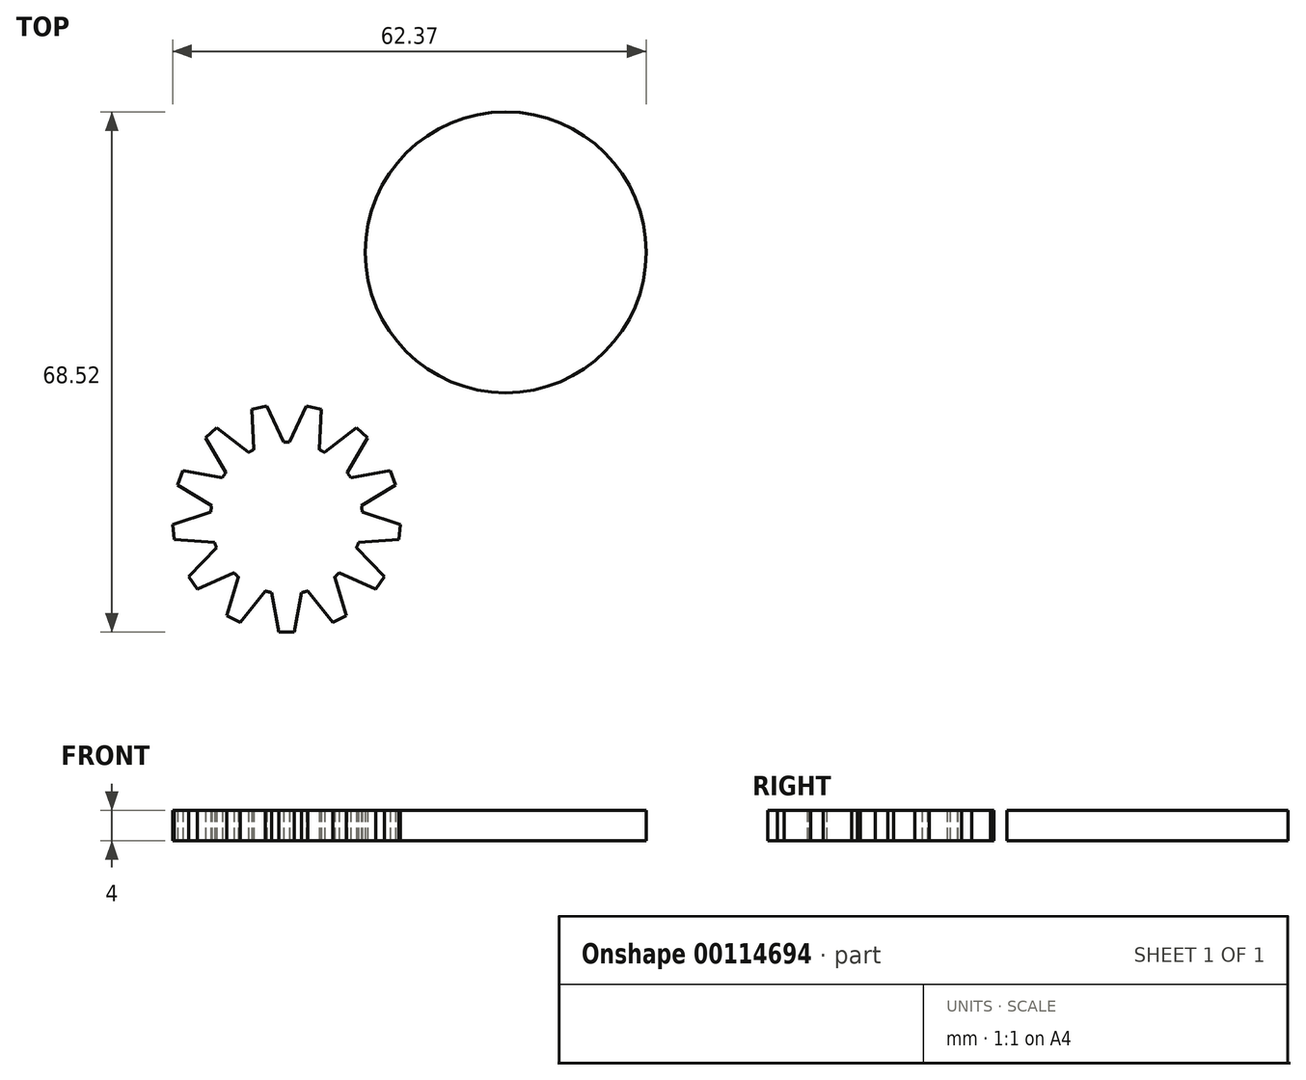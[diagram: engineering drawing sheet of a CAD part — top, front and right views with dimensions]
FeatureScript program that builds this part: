
annotation { "Feature Type Name" : "Feature", "Feature Type Description" : "" }
export const myFeature = defineFeature(function(context is Context, id is Id, definition is map)
    precondition{}
    {
        {
            var Q0;
            Q0=qCreatedBy(makeId("Top.planeOp"),FACE);
            var sketch = newSketch(context, id + "F0", { "sketchPlane" : qUnion([Q0])});
            skCircle(sketch, "E0", {"center": v(0, 0) * mm, "radius": 10 * mm});
            skLineSegment(sketch, "E1", {"start": v(0, -10) * mm, "end": v(0, -15) * mm});
            skLineSegment(sketch, "E2", {"start": v(0, -15) * mm, "end": v(-1, -15) * mm});
            skLineSegment(sketch, "E3", {"start": v(-1, -15) * mm, "end": v(-2, -9.8) * mm});
            skLineSegment(sketch, "E4", {"start": v(0, -15) * mm, "end": v(1, -15) * mm});
            skLineSegment(sketch, "E5", {"start": v(1, -15) * mm, "end": v(2, -9.8) * mm});
            skLineSegment(sketch, "E6.1.0", {"start": v(6.09, -13.75) * mm, "end": v(2.78, -9.6) * mm});
            skLineSegment(sketch, "E6.1.1", {"start": v(7.86, -12.82) * mm, "end": v(6.32, -7.75) * mm});
            skLineSegment(sketch, "E6.1.2", {"start": v(6.97, -13.28) * mm, "end": v(7.86, -12.82) * mm});
            skLineSegment(sketch, "E6.1.3", {"start": v(6.97, -13.28) * mm, "end": v(6.09, -13.75) * mm});
            skLineSegment(sketch, "E6.2.0", {"start": v(11.78, -9.34) * mm, "end": v(6.93, -7.21) * mm});
            skLineSegment(sketch, "E6.2.1", {"start": v(12.91, -7.7) * mm, "end": v(9.2, -3.92) * mm});
            skLineSegment(sketch, "E6.2.2", {"start": v(12.34, -8.52) * mm, "end": v(12.91, -7.7) * mm});
            skLineSegment(sketch, "E6.2.3", {"start": v(12.34, -8.52) * mm, "end": v(11.78, -9.34) * mm});
            skLineSegment(sketch, "E6.3.0", {"start": v(14.77, -2.8) * mm, "end": v(9.49, -3.17) * mm});
            skLineSegment(sketch, "E6.3.1", {"start": v(15.01, -0.82) * mm, "end": v(9.97, 0.8) * mm});
            skLineSegment(sketch, "E6.3.2", {"start": v(14.9, -1.8) * mm, "end": v(15.01, -0.82) * mm});
            skLineSegment(sketch, "E6.3.3", {"start": v(14.9, -1.8) * mm, "end": v(14.77, -2.8) * mm});
            skLineSegment(sketch, "E6.4.0", {"start": v(14.38, 4.38) * mm, "end": v(9.87, 1.6) * mm});
            skLineSegment(sketch, "E6.4.1", {"start": v(13.67, 6.25) * mm, "end": v(8.45, 5.34) * mm});
            skLineSegment(sketch, "E6.4.2", {"start": v(14.03, 5.32) * mm, "end": v(13.67, 6.25) * mm});
            skLineSegment(sketch, "E6.4.3", {"start": v(14.03, 5.32) * mm, "end": v(14.38, 4.38) * mm});
            skLineSegment(sketch, "E6.5.0", {"start": v(10.7, 10.56) * mm, "end": v(8, 6) * mm});
            skLineSegment(sketch, "E6.5.1", {"start": v(9.2, 11.9) * mm, "end": v(5, 8.66) * mm});
            skLineSegment(sketch, "E6.5.2", {"start": v(9.95, 11.23) * mm, "end": v(9.2, 11.9) * mm});
            skLineSegment(sketch, "E6.5.3", {"start": v(9.95, 11.23) * mm, "end": v(10.7, 10.56) * mm});
            skLineSegment(sketch, "E6.6.0", {"start": v(4.56, 14.32) * mm, "end": v(4.29, 9.03) * mm});
            skLineSegment(sketch, "E6.6.1", {"start": v(2.62, 14.8) * mm, "end": v(0.4, 10) * mm});
            skLineSegment(sketch, "E6.6.2", {"start": v(3.59, 14.56) * mm, "end": v(2.62, 14.8) * mm});
            skLineSegment(sketch, "E6.6.3", {"start": v(3.59, 14.56) * mm, "end": v(4.56, 14.32) * mm});
            skLineSegment(sketch, "E6.7.0", {"start": v(-2.62, 14.8) * mm, "end": v(-0.4, 10) * mm});
            skLineSegment(sketch, "E6.7.1", {"start": v(-4.56, 14.32) * mm, "end": v(-4.29, 9.03) * mm});
            skLineSegment(sketch, "E6.7.2", {"start": v(-3.59, 14.56) * mm, "end": v(-4.56, 14.32) * mm});
            skLineSegment(sketch, "E6.7.3", {"start": v(-3.59, 14.56) * mm, "end": v(-2.62, 14.8) * mm});
            skLineSegment(sketch, "E6.8.0", {"start": v(-9.2, 11.9) * mm, "end": v(-5, 8.66) * mm});
            skLineSegment(sketch, "E6.8.1", {"start": v(-10.7, 10.56) * mm, "end": v(-8, 6) * mm});
            skLineSegment(sketch, "E6.8.2", {"start": v(-9.95, 11.23) * mm, "end": v(-10.7, 10.56) * mm});
            skLineSegment(sketch, "E6.8.3", {"start": v(-9.95, 11.23) * mm, "end": v(-9.2, 11.9) * mm});
            skLineSegment(sketch, "E6.9.0", {"start": v(-13.67, 6.25) * mm, "end": v(-8.45, 5.34) * mm});
            skLineSegment(sketch, "E6.9.1", {"start": v(-14.38, 4.38) * mm, "end": v(-9.87, 1.6) * mm});
            skLineSegment(sketch, "E6.9.2", {"start": v(-14.03, 5.32) * mm, "end": v(-14.38, 4.38) * mm});
            skLineSegment(sketch, "E6.9.3", {"start": v(-14.03, 5.32) * mm, "end": v(-13.67, 6.25) * mm});
            skLineSegment(sketch, "E7.1.10.0", {"start": v(-15.01, -0.82) * mm, "end": v(-9.97, 0.8) * mm});
            skLineSegment(sketch, "E7.3.10.0", {"start": v(-14.77, -2.8) * mm, "end": v(-9.49, -3.17) * mm});
            skLineSegment(sketch, "E7.6.10.0", {"start": v(-14.9, -1.8) * mm, "end": v(-14.77, -2.8) * mm});
            skLineSegment(sketch, "E7.9.10.0", {"start": v(-14.9, -1.8) * mm, "end": v(-15.01, -0.82) * mm});
            skLineSegment(sketch, "E7.1.11.0", {"start": v(-12.91, -7.7) * mm, "end": v(-9.2, -3.92) * mm});
            skLineSegment(sketch, "E7.3.11.0", {"start": v(-11.78, -9.34) * mm, "end": v(-6.93, -7.21) * mm});
            skLineSegment(sketch, "E7.6.11.0", {"start": v(-12.34, -8.52) * mm, "end": v(-11.78, -9.34) * mm});
            skLineSegment(sketch, "E7.9.11.0", {"start": v(-12.34, -8.52) * mm, "end": v(-12.91, -7.7) * mm});
            skLineSegment(sketch, "E8.1.12.0", {"start": v(-7.86, -12.82) * mm, "end": v(-6.32, -7.75) * mm});
            skLineSegment(sketch, "E8.3.12.0", {"start": v(-6.09, -13.75) * mm, "end": v(-2.78, -9.6) * mm});
            skLineSegment(sketch, "E8.6.12.0", {"start": v(-6.97, -13.28) * mm, "end": v(-6.09, -13.75) * mm});
            skLineSegment(sketch, "E8.9.12.0", {"start": v(-6.97, -13.28) * mm, "end": v(-7.86, -12.82) * mm});
            skCircle(sketch, "E9", {"center": v(28.86, 35.02) * mm, "radius": 18.5 * mm});
            skSolve(sketch);
        }
        {
            var Q0;
            Q0 = qSketchRegion(id + "F0", true);
            extrude(context, id + "F1", {"entities" : qUnion([Q0]), "depth" : 4 * mm});
        }
    });
